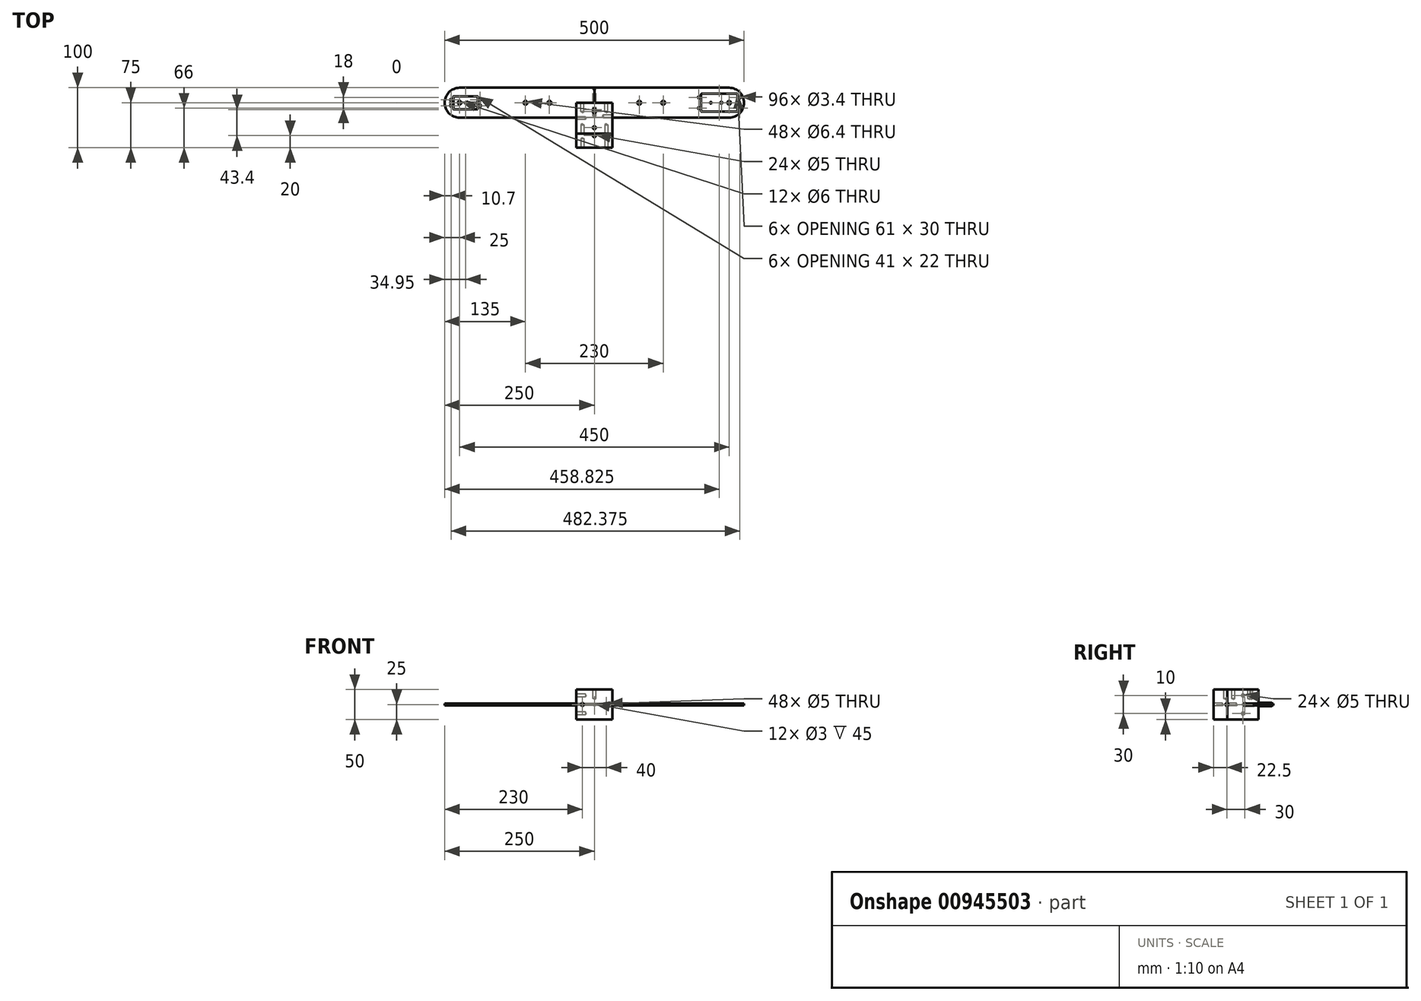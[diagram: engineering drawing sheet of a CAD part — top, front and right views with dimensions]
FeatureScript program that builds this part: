
annotation { "Feature Type Name" : "Feature", "Feature Type Description" : "" }
export const myFeature = defineFeature(function(context is Context, id is Id, definition is map)
    precondition{}
    {
        {
            var Q0;
            Q0=qCreatedBy(makeId("Top.planeOp"),FACE);
            var sketch = newSketch(context, id + "F0", { "sketchPlane" : qUnion([Q0])});
            skLineSegment(sketch, "E0.bottom", {"start": v(225, 25) * mm, "end": v(-225, 25) * mm});
            skLineSegment(sketch, "E0.top", {"start": v(225, -25) * mm, "end": v(-225, -25) * mm});
            skLineSegment(sketch, "E0.left", {"start": v(250, 0) * mm, "end": v(250, 0) * mm});
            skLineSegment(sketch, "E0.right", {"start": v(-250, 0) * mm, "end": v(-250, 0) * mm});
            skPoint(sketch, "E0.middle", {"position": v(0, 0) * mm});
            skPoint(sketch, "E1.visualSharp", {"position": v(250, 25) * mm});
            skArc(sketch, "E1.filletArc", {"start": v(250, 0) * mm, "mid": v(242.68, 17.68) * mm, "end": v(225, 25) * mm});
            skPoint(sketch, "E2.visualSharp", {"position": v(250, -25) * mm});
            skArc(sketch, "E2.filletArc", {"start": v(225, -25) * mm, "mid": v(242.68, -17.68) * mm, "end": v(250, 0) * mm});
            skPoint(sketch, "E3.visualSharp", {"position": v(-250, 25) * mm});
            skArc(sketch, "E3.filletArc", {"start": v(-225, 25) * mm, "mid": v(-242.68, 17.68) * mm, "end": v(-250, 0) * mm});
            skPoint(sketch, "E4.visualSharp", {"position": v(-250, -25) * mm});
            skArc(sketch, "E4.filletArc", {"start": v(-250, 0) * mm, "mid": v(-242.68, -17.68) * mm, "end": v(-225, -25) * mm});
            skLineSegment(sketch, "E5.bottom", {"start": v(239.32, 15) * mm, "end": v(178.32, 15) * mm});
            skLineSegment(sketch, "E5.top", {"start": v(239.32, -15) * mm, "end": v(178.32, -15) * mm});
            skLineSegment(sketch, "E5.left", {"start": v(239.32, 15) * mm, "end": v(239.32, -15) * mm});
            skLineSegment(sketch, "E5.right", {"start": v(178.32, 15) * mm, "end": v(178.32, -15) * mm});
            skPoint(sketch, "E5.middle", {"position": v(208.82, 0) * mm});
            skCircle(sketch, "E6", {"center": v(174.57, 9) * mm, "radius": 1.7 * mm});
            skPoint(sketch, "E7", {"position": v(208.82, 15) * mm});
            skPoint(sketch, "E8", {"position": v(208.82, -15) * mm});
            skPoint(sketch, "E9", {"position": v(239.32, 0) * mm});
            skPoint(sketch, "E10", {"position": v(178.32, 0) * mm});
            skCircle(sketch, "E11.MirrorC", {"center": v(243.07, 9) * mm, "radius": 1.7 * mm});
            skCircle(sketch, "E12.MirrorC", {"center": v(174.57, -9) * mm, "radius": 1.7 * mm});
            skCircle(sketch, "E13.MirrorC", {"center": v(243.07, -9) * mm, "radius": 1.7 * mm});
            skCircle(sketch, "E14", {"center": v(225, 0) * mm, "radius": 8.81 * mm});
            skLineSegment(sketch, "E15", {"start": v(0, 25) * mm, "end": v(0, -25) * mm});
            skCircle(sketch, "E16", {"center": v(-115, 0) * mm, "radius": 3.2 * mm});
            skCircle(sketch, "E17", {"center": v(-75, 0) * mm, "radius": 3.2 * mm});
            skCircle(sketch, "E18", {"center": v(115, 0) * mm, "radius": 3.2 * mm});
            skCircle(sketch, "E19", {"center": v(75, 0) * mm, "radius": 3.2 * mm});
            skLineSegment(sketch, "E20.bottom", {"start": v(-235.55, 11) * mm, "end": v(-194.55, 11) * mm});
            skLineSegment(sketch, "E20.top", {"start": v(-235.55, -11) * mm, "end": v(-194.55, -11) * mm});
            skLineSegment(sketch, "E20.left", {"start": v(-235.55, 11) * mm, "end": v(-235.55, -11) * mm});
            skLineSegment(sketch, "E20.right", {"start": v(-194.55, 11) * mm, "end": v(-194.55, -11) * mm});
            skCircle(sketch, "E21", {"center": v(-239.3, 4.9) * mm, "radius": 1.7 * mm});
            skCircle(sketch, "E22", {"center": v(-239.3, -4.9) * mm, "radius": 1.7 * mm});
            skCircle(sketch, "E23", {"center": v(-190.8, 4.9) * mm, "radius": 1.7 * mm});
            skCircle(sketch, "E24", {"center": v(-190.8, -4.9) * mm, "radius": 1.7 * mm});
            skLineSegment(sketch, "E25", {"start": v(-215.05, 11) * mm, "end": v(-215.05, -11) * mm});
            skSolve(sketch);
        }
        {
            var Q0;
            Q0 = qSketchRegion(id + "F0", true);
            extrude(context, id + "F1", {"entities" : qUnion([Q0]), "depth" : 1.5 * mm, "offsetDistance" : 25 * mm});
        }
        {
            var Q0;
            Q0=qCreatedBy(makeId("Top.planeOp"),FACE);
            var sketch = newSketch(context, id + "F2", { "sketchPlane" : qUnion([Q0])});
            skLineSegment(sketch, "E26.bottom", {"start": v(225, -25) * mm, "end": v(-225, -25) * mm});
            skLineSegment(sketch, "E26.top", {"start": v(225, 25) * mm, "end": v(-225, 25) * mm});
            skLineSegment(sketch, "E26.left", {"start": v(250, 0) * mm, "end": v(250, 0) * mm});
            skLineSegment(sketch, "E26.right", {"start": v(-250, 0) * mm, "end": v(-250, 0) * mm});
            skPoint(sketch, "E26.middle", {"position": v(0, 0) * mm});
            skPoint(sketch, "E27.visualSharp", {"position": v(-250, 25) * mm});
            skArc(sketch, "E27.filletArc", {"start": v(-225, 25) * mm, "mid": v(-242.68, 17.68) * mm, "end": v(-250, 0) * mm});
            skPoint(sketch, "E28.visualSharp", {"position": v(-250, -25) * mm});
            skArc(sketch, "E28.filletArc", {"start": v(-250, 0) * mm, "mid": v(-242.68, -17.68) * mm, "end": v(-225, -25) * mm});
            skPoint(sketch, "E29.visualSharp", {"position": v(250, -25) * mm});
            skArc(sketch, "E29.filletArc", {"start": v(225, -25) * mm, "mid": v(242.68, -17.68) * mm, "end": v(250, 0) * mm});
            skPoint(sketch, "E30.visualSharp", {"position": v(250, 25) * mm});
            skArc(sketch, "E30.filletArc", {"start": v(250, 0) * mm, "mid": v(242.68, 17.68) * mm, "end": v(225, 25) * mm});
            skCircle(sketch, "E31", {"center": v(-225, 0) * mm, "radius": 3 * mm});
            skCircle(sketch, "E32", {"center": v(225, 0) * mm, "radius": 3 * mm});
            skCircle(sketch, "E33", {"center": v(-75, 0) * mm, "radius": 3.2 * mm});
            skCircle(sketch, "E34", {"center": v(-115, 0) * mm, "radius": 3.2 * mm});
            skCircle(sketch, "E35.MirrorC", {"center": v(75, 0) * mm, "radius": 3.2 * mm});
            skCircle(sketch, "E36.MirrorC", {"center": v(115, 0) * mm, "radius": 3.2 * mm});
            skCircle(sketch, "E37", {"center": v(243.08, 9) * mm, "radius": 1.7 * mm});
            skCircle(sketch, "E38", {"center": v(243.08, -9) * mm, "radius": 1.6 * mm});
            skCircle(sketch, "E39", {"center": v(174.58, 9) * mm, "radius": 1.7 * mm});
            skCircle(sketch, "E40", {"center": v(174.58, -9) * mm, "radius": 1.7 * mm});
            skCircle(sketch, "E41", {"center": v(212.1, 0) * mm, "radius": 1.7 * mm});
            skCircle(sketch, "E42", {"center": v(194.55, 0) * mm, "radius": 1.45 * mm});
            skCircle(sketch, "E43", {"center": v(-239.3, 4.9) * mm, "radius": 1.7 * mm});
            skCircle(sketch, "E44", {"center": v(-239.3, -4.9) * mm, "radius": 1.7 * mm});
            skCircle(sketch, "E45", {"center": v(-190.8, 4.9) * mm, "radius": 1.7 * mm});
            skCircle(sketch, "E46", {"center": v(-190.8, -4.9) * mm, "radius": 1.7 * mm});
            skCircle(sketch, "E47", {"center": v(-208.5, 0) * mm, "radius": 0.9 * mm});
            skCircle(sketch, "E48", {"center": v(-241.5, 0) * mm, "radius": 0.9 * mm});
            skCircle(sketch, "E49", {"center": v(-212.1, 0) * mm, "radius": 1.6 * mm});
            skCircle(sketch, "E50", {"center": v(-194.55, 0) * mm, "radius": 1.45 * mm});
            skSolve(sketch);
        }
        {
            var Q0;
            Q0 = qSketchRegion(id + "F2", true);
            extrude(context, id + "F3", {"entities" : qUnion([Q0]), "oppositeDirection" : true, "depth" : 1.5 * mm, "offsetDistance" : 25 * mm});
        }
        {
            var Q0;
            Q0=qCreatedBy(makeId("Front.planeOp"),FACE);
            var sketch = newSketch(context, id + "F4", { "sketchPlane" : qUnion([Q0])});
            skLineSegment(sketch, "E51.bottom", {"start": v(30, 25) * mm, "end": v(-30, 25) * mm});
            skLineSegment(sketch, "E51.top", {"start": v(30, -25) * mm, "end": v(-30, -25) * mm});
            skLineSegment(sketch, "E51.left", {"start": v(30, 25) * mm, "end": v(30, -25) * mm});
            skLineSegment(sketch, "E51.right", {"start": v(-30, 25) * mm, "end": v(-30, -25) * mm});
            skPoint(sketch, "E51.middle", {"position": v(0, 0) * mm});
            skPoint(sketch, "E52", {"position": v(-20, 0) * mm});
            skPoint(sketch, "E53", {"position": v(20, 0) * mm});
            skSolve(sketch);
        }
        {
            var Q0;
            Q0 = qSketchRegion(id + "F4", true);
            extrude(context, id + "F5", {"entities" : qUnion([Q0]), "depth" : (55 - 3.4) * mm, "offsetDistance" : 25 * mm});
        }
        {
            var Q0;
            Q0=qCreatedBy(makeId("Front.planeOp"),FACE);
            var sketch = newSketch(context, id + "F6", { "sketchPlane" : qUnion([Q0])});
            skLineSegment(sketch, "E54.bottom", {"start": v(30, 25) * mm, "end": v(-30, 25) * mm});
            skLineSegment(sketch, "E54.top", {"start": v(30, -25) * mm, "end": v(-30, -25) * mm});
            skLineSegment(sketch, "E54.left", {"start": v(30, 25) * mm, "end": v(30, -25) * mm});
            skLineSegment(sketch, "E54.right", {"start": v(-30, 25) * mm, "end": v(-30, -25) * mm});
            skPoint(sketch, "E54.middle", {"position": v(0, 0) * mm});
            skPoint(sketch, "E55", {"position": v(20, 0) * mm});
            skPoint(sketch, "E56", {"position": v(-20, 0) * mm});
            skSolve(sketch);
        }
        {
            var Q0;
            Q0 = qSketchRegion(id + "F6", true);
            extrude(context, id + "F7", {"entities" : qUnion([Q0]), "depth" : 75 * mm, "offsetDistance" : 25 * mm});
        }
        {
            var Q0;
            Q0=qCreatedBy(makeId("Front.planeOp"),FACE);
            var sketch = newSketch(context, id + "F8", { "sketchPlane" : qUnion([Q0])});
            skCircle(sketch, "E57.cCircle", {"center": v(0, 0) * mm, "radius": 2.5 * mm, "construction": true});
            skLineSegment(sketch, "E57.0", {"start": v(2.5, 1.44) * mm, "end": v(2.5, -1.44) * mm});
            skLineSegment(sketch, "E57.1", {"start": v(2.5, -1.44) * mm, "end": v(0, -2.89) * mm});
            skLineSegment(sketch, "E57.2", {"start": v(0, -2.89) * mm, "end": v(-2.5, -1.44) * mm});
            skLineSegment(sketch, "E57.3", {"start": v(-2.5, -1.44) * mm, "end": v(-2.5, 1.44) * mm});
            skLineSegment(sketch, "E57.4", {"start": v(-2.5, 1.44) * mm, "end": v(0, 2.89) * mm});
            skLineSegment(sketch, "E57.5", {"start": v(0, 2.89) * mm, "end": v(2.5, 1.44) * mm});
            skPoint(sketch, "E57.0.midPoint", {"position": v(2.5, 0) * mm});
            skCircle(sketch, "E58", {"center": v(0, 0) * mm, "radius": 1.5 * mm});
            skSolve(sketch);
        }
        {
            var Q0;
            Q0 = qSketchRegion(id + "F8", true);
            extrude(context, id + "F9", {"entities" : qUnion([Q0]), "endBound" : BoundingType.SYMMETRIC, "depth" : 45 * mm, "offsetDistance" : 25 * mm});
        }
        {
            var Q0;
            Q0=makeQuery(id+"F9.opExtrude","CAP_EDGE",EDGE,{"disambiguationData":[OSD([sQuery(id+"F8.wireOp",EDGE,"E57.4")])],"isStart":false});
            var Q1;
            Q1=makeQuery(id+"F9.opExtrude","CAP_EDGE",EDGE,{"disambiguationData":[OSD([sQuery(id+"F8.wireOp",EDGE,"E57.5")])],"isStart":false});
            var Q2;
            Q2=makeQuery(id+"F9.opExtrude","CAP_EDGE",EDGE,{"disambiguationData":[OSD([sQuery(id+"F8.wireOp",EDGE,"E57.0")])],"isStart":false});
            var Q3;
            Q3=makeQuery(id+"F9.opExtrude","CAP_EDGE",EDGE,{"disambiguationData":[OSD([sQuery(id+"F8.wireOp",EDGE,"E57.1")])],"isStart":false});
            var Q4;
            Q4=makeQuery(id+"F9.opExtrude","CAP_EDGE",EDGE,{"disambiguationData":[OSD([sQuery(id+"F8.wireOp",EDGE,"E57.2")])],"isStart":false});
            var Q5;
            Q5=makeQuery(id+"F9.opExtrude","CAP_EDGE",EDGE,{"disambiguationData":[OSD([sQuery(id+"F8.wireOp",EDGE,"E57.3")])],"isStart":false});
            var Q6;
            Q6=makeQuery(id+"F9.opExtrude","CAP_EDGE",EDGE,{"disambiguationData":[OSD([sQuery(id+"F8.wireOp",EDGE,"E57.5")])],"isStart":true});
            var Q7;
            Q7=makeQuery(id+"F9.opExtrude","CAP_EDGE",EDGE,{"disambiguationData":[OSD([sQuery(id+"F8.wireOp",EDGE,"E57.4")])],"isStart":true});
            var Q8;
            Q8=makeQuery(id+"F9.opExtrude","CAP_EDGE",EDGE,{"disambiguationData":[OSD([sQuery(id+"F8.wireOp",EDGE,"E57.3")])],"isStart":true});
            var Q9;
            Q9=makeQuery(id+"F9.opExtrude","CAP_EDGE",EDGE,{"disambiguationData":[OSD([sQuery(id+"F8.wireOp",EDGE,"E57.2")])],"isStart":true});
            var Q10;
            Q10=makeQuery(id+"F9.opExtrude","CAP_EDGE",EDGE,{"disambiguationData":[OSD([sQuery(id+"F8.wireOp",EDGE,"E57.1")])],"isStart":true});
            var Q11;
            Q11=makeQuery(id+"F9.opExtrude","CAP_EDGE",EDGE,{"disambiguationData":[OSD([sQuery(id+"F8.wireOp",EDGE,"E57.0")])],"isStart":true});
            fillet(context, id + "F10", {"entities" : qUnion([Q0, Q1, Q2, Q3, Q4, Q5, Q6, Q7, Q8, Q9, Q10, Q11]), "radius" : 0.5 * mm, "tangentPropagation" : true, "allowEdgeOverflow" : false});
        }
        {
            var Q0;
            Q0=qCreatedBy(makeId("Front.planeOp"),FACE);
            var sketch = newSketch(context, id + "F11", { "sketchPlane" : qUnion([Q0])});
            skCircle(sketch, "E59.cCircle", {"center": v(0, 0) * mm, "radius": 2.5 * mm, "construction": true});
            skLineSegment(sketch, "E59.0", {"start": v(0, 2.89) * mm, "end": v(2.5, 1.44) * mm});
            skLineSegment(sketch, "E59.1", {"start": v(2.5, 1.44) * mm, "end": v(2.5, -1.44) * mm});
            skLineSegment(sketch, "E59.2", {"start": v(2.5, -1.44) * mm, "end": v(0, -2.89) * mm});
            skLineSegment(sketch, "E59.3", {"start": v(0, -2.89) * mm, "end": v(-2.5, -1.44) * mm});
            skLineSegment(sketch, "E59.4", {"start": v(-2.5, -1.44) * mm, "end": v(-2.5, 1.44) * mm});
            skLineSegment(sketch, "E59.5", {"start": v(-2.5, 1.44) * mm, "end": v(0, 2.89) * mm});
            skPoint(sketch, "E59.0.midPoint", {"position": v(1.25, 2.17) * mm});
            skCircle(sketch, "E60", {"center": v(0, 0) * mm, "radius": 1.5 * mm});
            skSolve(sketch);
        }
        {
            var Q0;
            Q0 = qSketchRegion(id + "F11", true);
            extrude(context, id + "F12", {"entities" : qUnion([Q0]), "endBound" : BoundingType.SYMMETRIC, "depth" : 45 * mm, "offsetDistance" : 25 * mm});
        }
        {
            var Q0;
            Q0=makeQuery(id+"F12.opExtrude","CAP_EDGE",EDGE,{"disambiguationData":[OSD([sQuery(id+"F11.wireOp",EDGE,"E59.5")])],"isStart":false});
            var Q1;
            Q1=makeQuery(id+"F12.opExtrude","CAP_EDGE",EDGE,{"disambiguationData":[OSD([sQuery(id+"F11.wireOp",EDGE,"E59.0")])],"isStart":false});
            var Q2;
            Q2=makeQuery(id+"F12.opExtrude","CAP_EDGE",EDGE,{"disambiguationData":[OSD([sQuery(id+"F11.wireOp",EDGE,"E59.1")])],"isStart":false});
            var Q3;
            Q3=makeQuery(id+"F12.opExtrude","CAP_EDGE",EDGE,{"disambiguationData":[OSD([sQuery(id+"F11.wireOp",EDGE,"E59.2")])],"isStart":false});
            var Q4;
            Q4=makeQuery(id+"F12.opExtrude","CAP_EDGE",EDGE,{"disambiguationData":[OSD([sQuery(id+"F11.wireOp",EDGE,"E59.3")])],"isStart":false});
            var Q5;
            Q5=makeQuery(id+"F12.opExtrude","CAP_EDGE",EDGE,{"disambiguationData":[OSD([sQuery(id+"F11.wireOp",EDGE,"E59.4")])],"isStart":false});
            var Q6;
            Q6=makeQuery(id+"F12.opExtrude","CAP_EDGE",EDGE,{"disambiguationData":[OSD([sQuery(id+"F11.wireOp",EDGE,"E59.0")])],"isStart":true});
            var Q7;
            Q7=makeQuery(id+"F12.opExtrude","CAP_EDGE",EDGE,{"disambiguationData":[OSD([sQuery(id+"F11.wireOp",EDGE,"E59.5")])],"isStart":true});
            var Q8;
            Q8=makeQuery(id+"F12.opExtrude","CAP_EDGE",EDGE,{"disambiguationData":[OSD([sQuery(id+"F11.wireOp",EDGE,"E59.4")])],"isStart":true});
            var Q9;
            Q9=makeQuery(id+"F12.opExtrude","CAP_EDGE",EDGE,{"disambiguationData":[OSD([sQuery(id+"F11.wireOp",EDGE,"E59.3")])],"isStart":true});
            var Q10;
            Q10=makeQuery(id+"F12.opExtrude","CAP_EDGE",EDGE,{"disambiguationData":[OSD([sQuery(id+"F11.wireOp",EDGE,"E59.2")])],"isStart":true});
            var Q11;
            Q11=makeQuery(id+"F12.opExtrude","CAP_EDGE",EDGE,{"disambiguationData":[OSD([sQuery(id+"F11.wireOp",EDGE,"E59.1")])],"isStart":true});
            fillet(context, id + "F13", {"entities" : qUnion([Q0, Q1, Q2, Q3, Q4, Q5, Q6, Q7, Q8, Q9, Q10, Q11]), "radius" : 0.5 * mm, "tangentPropagation" : true, "allowEdgeOverflow" : false});
        }
        {
            var Q0;
            Q0=makeQuery(id+"F5.opExtrude","SWEPT_FACE",FACE,{"disambiguationData":[OSD([sQuery(id+"F4.wireOp",EDGE,"E51.bottom")])]});
            var sketch = newSketch(context, id + "F14", { "sketchPlane" : qUnion([Q0])});
            skPoint(sketch, "E61", {"position": v(0, -11.6) * mm});
            skPoint(sketch, "E62", {"position": v(0, -41.6) * mm});
            skSolve(sketch);
        }
        {
            var Q0;
            Q0=sQuery(id+"F14.wireOp",VERTEX,"E61");
            var Q1;
            Q1=sQuery(id+"F14.wireOp",VERTEX,"E62");
            var Q2;
            Q2=makeQuery(id+"F5.opExtrude","SWEPT_BODY",BODY,{"disambiguationData":[OSD([sQuery(id+"F4.wireOp",EDGE,"E51.bottom"),sQuery(id+"F4.wireOp",EDGE,"E51.top"),sQuery(id+"F4.wireOp",EDGE,"E51.left"),sQuery(id+"F4.wireOp",EDGE,"E51.right"),sQuery(id+"F4.wireOp",EDGE,"B9JAuCr5-AHYt-nNv3-OBoy-IqFfUuk4iHH8"),sQuery(id+"F4.wireOp",EDGE,"3c7379fd-6569-4377-9c91-1a52de3556030.MirrorC")])]});
            hole(context, id + "F15", {"style" : HoleStyle.SIMPLE, "endStyle" : HoleEndStyle.BLIND, "standardTappedOrClearance" : lookupTablePath({ "standard" : "ISO", "engagement" : "75%", "pitch" : "1 mm", "size" : "M6", "type" : "Tapped" }), "standardBlindInLast" : lookupTablePath({ "standard" : "ISO", "fit" : "Normal", "engagement" : "75%", "pitch" : "1 mm", "size" : "M6", "type" : "Clearance & tapped" }), "holeDiameter" : 5 * mm, "majorDiameter" : 6 * mm, "showTappedDepth" : true, "holeDepth" : 15 * mm, "isTappedThrough" : true, "tappedDepth" : 12 * mm, "tapClearance" : 3, "startFromSketch" : true, "locations" : qUnion([Q0, Q1]), "scope" : qUnion([Q2])});
        }
        {
            var Q0;
            Q0=makeQuery(id+"F5.opExtrude","SWEPT_FACE",FACE,{"disambiguationData":[OSD([sQuery(id+"F4.wireOp",EDGE,"E51.right")])]});
            var sketch = newSketch(context, id + "F16", { "sketchPlane" : qUnion([Q0])});
            skPoint(sketch, "E63", {"position": v(25.8, 15) * mm});
            skPoint(sketch, "E64", {"position": v(25.8, -15) * mm});
            skLineSegment(sketch, "E65", {"start": v(25.8, 25) * mm, "end": v(25.8, -25) * mm});
            skSolve(sketch);
        }
        {
            var Q0;
            Q0=sQuery(id+"F16.wireOp",VERTEX,"E63");
            var Q1;
            Q1=sQuery(id+"F16.wireOp",VERTEX,"E64");
            var Q2;
            Q2=makeQuery(id+"F5.opExtrude","SWEPT_BODY",BODY,{"disambiguationData":[OSD([sQuery(id+"F4.wireOp",EDGE,"E51.bottom"),sQuery(id+"F4.wireOp",EDGE,"E51.top"),sQuery(id+"F4.wireOp",EDGE,"E51.left"),sQuery(id+"F4.wireOp",EDGE,"E51.right"),sQuery(id+"F4.wireOp",EDGE,"B9JAuCr5-AHYt-nNv3-OBoy-IqFfUuk4iHH8"),sQuery(id+"F4.wireOp",EDGE,"3c7379fd-6569-4377-9c91-1a52de3556030.MirrorC")])]});
            hole(context, id + "F17", {"style" : HoleStyle.SIMPLE, "endStyle" : HoleEndStyle.BLIND, "standardTappedOrClearance" : lookupTablePath({ "standard" : "ISO", "engagement" : "75%", "pitch" : "1 mm", "size" : "M6", "type" : "Tapped" }), "standardBlindInLast" : lookupTablePath({ "standard" : "ISO", "fit" : "Normal", "engagement" : "75%", "pitch" : "1 mm", "size" : "M6", "type" : "Clearance & tapped" }), "holeDiameter" : 5 * mm, "majorDiameter" : 6 * mm, "showTappedDepth" : true, "holeDepth" : 15 * mm, "isTappedThrough" : true, "tappedDepth" : 12 * mm, "tapClearance" : 3, "startFromSketch" : true, "locations" : qUnion([Q0, Q1]), "scope" : qUnion([Q2])});
        }
        {
            var Q0;
            Q0=makeQuery(id+"F7.opExtrude","SWEPT_FACE",FACE,{"disambiguationData":[OSD([sQuery(id+"F6.wireOp",EDGE,"E54.bottom")])]});
            var sketch = newSketch(context, id + "F18", { "sketchPlane" : qUnion([Q0])});
            skPoint(sketch, "E66", {"position": v(0, -15) * mm});
            skPoint(sketch, "E67", {"position": v(0, -55) * mm});
            skSolve(sketch);
        }
        {
            var Q0;
            Q0=sQuery(id+"F18.wireOp",VERTEX,"E66");
            var Q1;
            Q1=sQuery(id+"F18.wireOp",VERTEX,"E67");
            var Q2;
            Q2=makeQuery(id+"F7.opExtrude","SWEPT_BODY",BODY,{"disambiguationData":[OSD([sQuery(id+"F6.wireOp",EDGE,"E54.bottom"),sQuery(id+"F6.wireOp",EDGE,"E54.top"),sQuery(id+"F6.wireOp",EDGE,"E54.left"),sQuery(id+"F6.wireOp",EDGE,"E54.right"),sQuery(id+"F6.wireOp",EDGE,"4ATIYYtb-8uSl-pjGR-gpFR-P5wqYazPzhVi"),sQuery(id+"F6.wireOp",EDGE,"10c65846-2768-41ee-a349-169c0eae04130.MirrorC")])]});
            hole(context, id + "F19", {"style" : HoleStyle.SIMPLE, "endStyle" : HoleEndStyle.BLIND, "standardTappedOrClearance" : lookupTablePath({ "standard" : "ISO", "engagement" : "75%", "pitch" : "1 mm", "size" : "M6", "type" : "Tapped" }), "standardBlindInLast" : lookupTablePath({ "standard" : "ISO", "fit" : "Normal", "engagement" : "75%", "pitch" : "1 mm", "size" : "M6", "type" : "Clearance & tapped" }), "holeDiameter" : 5 * mm, "majorDiameter" : 6 * mm, "showTappedDepth" : true, "holeDepth" : 15 * mm, "isTappedThrough" : true, "tappedDepth" : 12 * mm, "tapClearance" : 3, "startFromSketch" : true, "locations" : qUnion([Q0, Q1]), "scope" : qUnion([Q2])});
        }
        {
            var Q0;
            Q0=makeQuery(id+"F7.opExtrude","SWEPT_FACE",FACE,{"disambiguationData":[OSD([sQuery(id+"F6.wireOp",EDGE,"E54.left")])]});
            var sketch = newSketch(context, id + "F20", { "sketchPlane" : qUnion([Q0])});
            skPoint(sketch, "E68", {"position": v(-52.5, 0) * mm});
            skPoint(sketch, "E69", {"position": v(-22.5, 0) * mm});
            skSolve(sketch);
        }
        {
            var Q0;
            Q0=sQuery(id+"F20.wireOp",VERTEX,"E69");
            var Q1;
            Q1=sQuery(id+"F20.wireOp",VERTEX,"E68");
            var Q2;
            Q2=makeQuery(id+"F7.opExtrude","SWEPT_BODY",BODY,{"disambiguationData":[OSD([sQuery(id+"F6.wireOp",EDGE,"E54.bottom"),sQuery(id+"F6.wireOp",EDGE,"E54.top"),sQuery(id+"F6.wireOp",EDGE,"E54.left"),sQuery(id+"F6.wireOp",EDGE,"E54.right"),sQuery(id+"F6.wireOp",EDGE,"4ATIYYtb-8uSl-pjGR-gpFR-P5wqYazPzhVi"),sQuery(id+"F6.wireOp",EDGE,"10c65846-2768-41ee-a349-169c0eae04130.MirrorC")])]});
            hole(context, id + "F21", {"style" : HoleStyle.SIMPLE, "endStyle" : HoleEndStyle.BLIND, "standardTappedOrClearance" : lookupTablePath({ "standard" : "ISO", "engagement" : "75%", "pitch" : "1 mm", "size" : "M6", "type" : "Tapped" }), "standardBlindInLast" : lookupTablePath({ "standard" : "ISO", "fit" : "Normal", "engagement" : "75%", "pitch" : "1 mm", "size" : "M6", "type" : "Clearance & tapped" }), "holeDiameter" : 5 * mm, "majorDiameter" : 6 * mm, "showTappedDepth" : true, "holeDepth" : 15 * mm, "isTappedThrough" : true, "tappedDepth" : 12 * mm, "tapClearance" : 3, "startFromSketch" : true, "locations" : qUnion([Q0, Q1]), "scope" : qUnion([Q2])});
        }
        {
            var Q0;
            Q0=sQuery(id+"F4.wireOp",VERTEX,"E52");
            var Q1;
            Q1=sQuery(id+"F4.wireOp",VERTEX,"E53");
            var Q2;
            Q2=makeQuery(id+"F5.opExtrude","SWEPT_BODY",BODY,{"disambiguationData":[OSD([sQuery(id+"F4.wireOp",EDGE,"E51.bottom"),sQuery(id+"F4.wireOp",EDGE,"E51.top"),sQuery(id+"F4.wireOp",EDGE,"E51.left"),sQuery(id+"F4.wireOp",EDGE,"E51.right")])]});
            hole(context, id + "F22", {"style" : HoleStyle.SIMPLE, "endStyle" : HoleEndStyle.BLIND, "oppositeDirection" : true, "standardTappedOrClearance" : lookupTablePath({ "standard" : "ISO", "engagement" : "75%", "pitch" : "1 mm", "size" : "M6", "type" : "Tapped" }), "standardBlindInLast" : lookupTablePath({ "standard" : "ISO", "fit" : "Normal", "engagement" : "75%", "pitch" : "1 mm", "size" : "M6", "type" : "Clearance & tapped" }), "holeDiameter" : 5 * mm, "majorDiameter" : 6 * mm, "showTappedDepth" : true, "holeDepth" : 15 * mm, "isTappedThrough" : true, "tappedDepth" : 12 * mm, "tapClearance" : 3, "startFromSketch" : true, "locations" : qUnion([Q0, Q1]), "scope" : qUnion([Q2])});
        }
        {
            var Q0;
            Q0=makeQuery(id+"F5.opExtrude","CAP_FACE",FACE,{"disambiguationData":[OSD([sQuery(id+"F4.wireOp",EDGE,"E51.bottom"),sQuery(id+"F4.wireOp",EDGE,"E51.top"),sQuery(id+"F4.wireOp",EDGE,"E51.left"),sQuery(id+"F4.wireOp",EDGE,"E51.right")])],"isStart":false});
            var sketch = newSketch(context, id + "F23", { "sketchPlane" : qUnion([Q0])});
            skPoint(sketch, "E70", {"position": v(-20, 0) * mm});
            skPoint(sketch, "E71", {"position": v(20, 0) * mm});
            skSolve(sketch);
        }
        {
            var Q0;
            Q0=sQuery(id+"F23.wireOp",VERTEX,"E70");
            var Q1;
            Q1=sQuery(id+"F23.wireOp",VERTEX,"E71");
            var Q2;
            Q2=makeQuery(id+"F5.opExtrude","SWEPT_BODY",BODY,{"disambiguationData":[OSD([sQuery(id+"F4.wireOp",EDGE,"E51.bottom"),sQuery(id+"F4.wireOp",EDGE,"E51.top"),sQuery(id+"F4.wireOp",EDGE,"E51.left"),sQuery(id+"F4.wireOp",EDGE,"E51.right")])]});
            hole(context, id + "F24", {"style" : HoleStyle.SIMPLE, "endStyle" : HoleEndStyle.BLIND, "standardTappedOrClearance" : lookupTablePath({ "standard" : "ISO", "engagement" : "75%", "pitch" : "1 mm", "size" : "M6", "type" : "Tapped" }), "standardBlindInLast" : lookupTablePath({ "standard" : "ISO", "fit" : "Normal", "engagement" : "75%", "pitch" : "1 mm", "size" : "M6", "type" : "Clearance & tapped" }), "holeDiameter" : 5 * mm, "majorDiameter" : 6 * mm, "showTappedDepth" : true, "holeDepth" : 15 * mm, "isTappedThrough" : true, "tappedDepth" : 12 * mm, "tapClearance" : 3, "locations" : qUnion([Q0, Q1]), "scope" : qUnion([Q2])});
        }
        {
            var Q0;
            Q0=sQuery(id+"F6.wireOp",VERTEX,"E55");
            var Q1;
            Q1=sQuery(id+"F6.wireOp",VERTEX,"E56");
            var Q2;
            Q2=makeQuery(id+"F7.opExtrude","SWEPT_BODY",BODY,{"disambiguationData":[OSD([sQuery(id+"F6.wireOp",EDGE,"E54.bottom"),sQuery(id+"F6.wireOp",EDGE,"E54.top"),sQuery(id+"F6.wireOp",EDGE,"E54.left"),sQuery(id+"F6.wireOp",EDGE,"E54.right")])]});
            hole(context, id + "F25", {"style" : HoleStyle.SIMPLE, "endStyle" : HoleEndStyle.BLIND, "oppositeDirection" : true, "standardTappedOrClearance" : lookupTablePath({ "standard" : "ISO", "engagement" : "75%", "pitch" : "1 mm", "size" : "M6", "type" : "Tapped" }), "standardBlindInLast" : lookupTablePath({ "standard" : "ISO", "fit" : "Normal", "engagement" : "75%", "pitch" : "1 mm", "size" : "M6", "type" : "Clearance & tapped" }), "holeDiameter" : 5 * mm, "majorDiameter" : 6 * mm, "showTappedDepth" : true, "holeDepth" : 15 * mm, "isTappedThrough" : true, "tappedDepth" : 12 * mm, "tapClearance" : 3, "locations" : qUnion([Q0, Q1]), "scope" : qUnion([Q2])});
        }
        {
            var Q0;
            Q0=makeQuery(id+"F7.opExtrude","CAP_FACE",FACE,{"disambiguationData":[OSD([sQuery(id+"F6.wireOp",EDGE,"E54.bottom"),sQuery(id+"F6.wireOp",EDGE,"E54.top"),sQuery(id+"F6.wireOp",EDGE,"E54.left"),sQuery(id+"F6.wireOp",EDGE,"E54.right")])],"isStart":false});
            var sketch = newSketch(context, id + "F26", { "sketchPlane" : qUnion([Q0])});
            skPoint(sketch, "E72", {"position": v(-20, 0) * mm});
            skPoint(sketch, "E73", {"position": v(20, 0) * mm});
            skSolve(sketch);
        }
        {
            var Q0;
            Q0=sQuery(id+"F26.wireOp",VERTEX,"E72");
            var Q1;
            Q1=sQuery(id+"F26.wireOp",VERTEX,"E73");
            var Q2;
            Q2=makeQuery(id+"F7.opExtrude","SWEPT_BODY",BODY,{"disambiguationData":[OSD([sQuery(id+"F6.wireOp",EDGE,"E54.bottom"),sQuery(id+"F6.wireOp",EDGE,"E54.top"),sQuery(id+"F6.wireOp",EDGE,"E54.left"),sQuery(id+"F6.wireOp",EDGE,"E54.right")])]});
            hole(context, id + "F27", {"style" : HoleStyle.SIMPLE, "endStyle" : HoleEndStyle.BLIND, "standardTappedOrClearance" : lookupTablePath({ "standard" : "ISO", "engagement" : "75%", "pitch" : "1 mm", "size" : "M6", "type" : "Tapped" }), "standardBlindInLast" : lookupTablePath({ "standard" : "ISO", "fit" : "Normal", "engagement" : "75%", "pitch" : "1 mm", "size" : "M6", "type" : "Clearance & tapped" }), "holeDiameter" : 5 * mm, "majorDiameter" : 6 * mm, "showTappedDepth" : true, "holeDepth" : 15 * mm, "isTappedThrough" : true, "tappedDepth" : 12 * mm, "tapClearance" : 3, "locations" : qUnion([Q0, Q1]), "scope" : qUnion([Q2])});
        }
        {
            var Q0;
            Q0=makeQuery(id+"F1.opExtrude","SWEPT_EDGE",EDGE,{"disambiguationData":[OSD([sQuery(id+"F0.wireOp",EDGE,"E20.bottom"),sQuery(id+"F0.wireOp",EDGE,"E20.left")])]});
            var Q1;
            Q1=makeQuery(id+"F1.opExtrude","SWEPT_EDGE",EDGE,{"disambiguationData":[OSD([sQuery(id+"F0.wireOp",EDGE,"E20.top"),sQuery(id+"F0.wireOp",EDGE,"E20.left")])]});
            var Q2;
            Q2=makeQuery(id+"F1.opExtrude","SWEPT_EDGE",EDGE,{"disambiguationData":[OSD([sQuery(id+"F0.wireOp",EDGE,"E20.top"),sQuery(id+"F0.wireOp",EDGE,"E20.right")])]});
            var Q3;
            Q3=makeQuery(id+"F1.opExtrude","SWEPT_EDGE",EDGE,{"disambiguationData":[OSD([sQuery(id+"F0.wireOp",EDGE,"E20.bottom"),sQuery(id+"F0.wireOp",EDGE,"E20.right")])]});
            var Q4;
            Q4=makeQuery(id+"F1.opExtrude","SWEPT_EDGE",EDGE,{"disambiguationData":[OSD([sQuery(id+"F0.wireOp",EDGE,"E5.bottom"),sQuery(id+"F0.wireOp",EDGE,"E5.right")])]});
            var Q5;
            Q5=makeQuery(id+"F1.opExtrude","SWEPT_EDGE",EDGE,{"disambiguationData":[OSD([sQuery(id+"F0.wireOp",EDGE,"E5.top"),sQuery(id+"F0.wireOp",EDGE,"E5.right")])]});
            var Q6;
            Q6=makeQuery(id+"F1.opExtrude","SWEPT_EDGE",EDGE,{"disambiguationData":[OSD([sQuery(id+"F0.wireOp",EDGE,"E5.top"),sQuery(id+"F0.wireOp",EDGE,"E5.left")])]});
            var Q7;
            Q7=makeQuery(id+"F1.opExtrude","SWEPT_EDGE",EDGE,{"disambiguationData":[OSD([sQuery(id+"F0.wireOp",EDGE,"E5.bottom"),sQuery(id+"F0.wireOp",EDGE,"E5.left")])]});
            fillet(context, id + "F28", {"entities" : qUnion([Q0, Q1, Q2, Q3, Q4, Q5, Q6, Q7]), "radius" : 0.5 * mm, "tangentPropagation" : true, "allowEdgeOverflow" : false});
        }
    });
